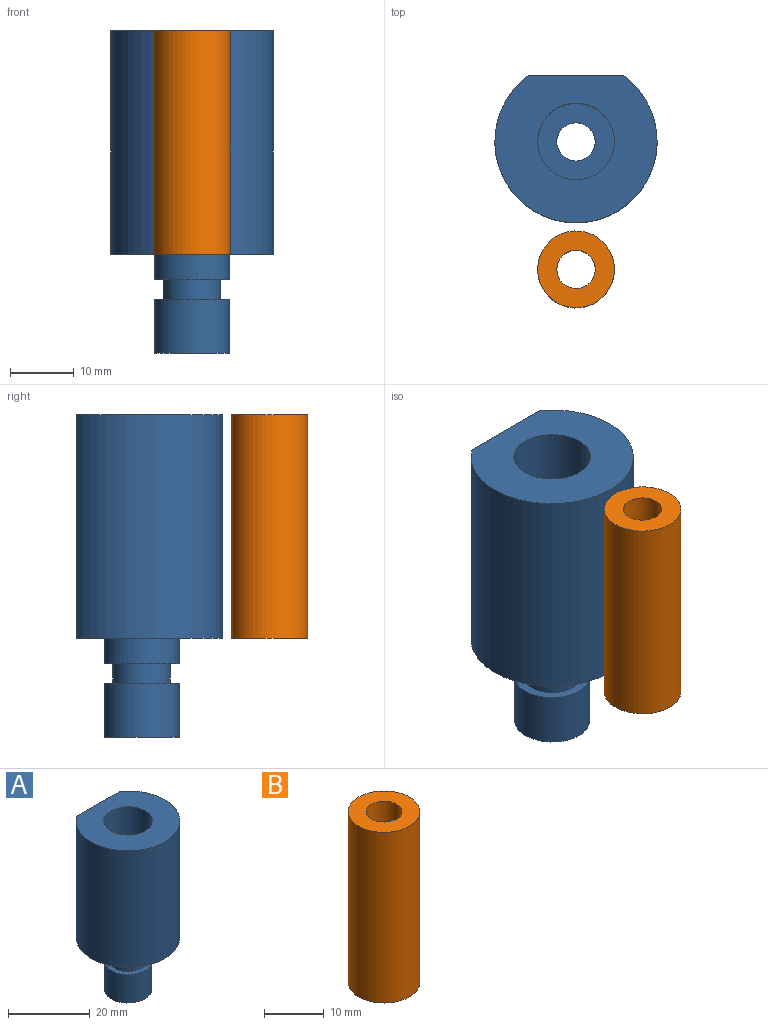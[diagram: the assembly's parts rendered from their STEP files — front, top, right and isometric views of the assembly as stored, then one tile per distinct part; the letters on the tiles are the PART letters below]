
ASSEMBLY  parts=2 mates=1
PART A: 14 faces, bbox 25.4x22.9x50.5 mm
  f0: cylinder r=12.7mm len=35mm, axis (0,0,-1), area 2231.3mm2, adj f1,f2,f13
  f1: plane 25.4x22.95mm, normal (0,0,1), area 368.6mm2, adj f0,f5,f13
  f2: plane 25.4x22.95mm, normal (0,0,-1), area 373.2mm2, adj f0,f7,f13
  f3: cylinder r=4.55mm len=9.1mm, axis (0,-1,0), area 149.8mm2, adj f5,f13
  f4: cylinder r=5.88mm len=11.75mm, axis (0,0,1), area 313.8mm2, adj f8,f10
  f5: cylinder r=6mm len=32mm, axis (0,0,1), area 1135.1mm2, adj f1,f3,f6
  f6: plane 12x12mm, normal (0,0,1), area 84.8mm2, adj f5,f9
  f7: cylinder r=5.88mm len=11.75mm, axis (0,0,1), area 147.7mm2, adj f2,f12
  f8: plane 11.75x11.75mm, normal (0,0,-1), area 80.2mm2, adj f4,f9
  f9: cylinder r=3mm len=18.5mm, axis (0,0,-1), area 348.7mm2, adj f6,f8
  f10: plane 11.75x11.75mm, normal (0,0,1), area 44.8mm2, adj f4,f11
  f11: cylinder r=4.5mm len=9mm, axis (0,0,-1), area 84.8mm2, adj f10,f12
  f12: plane 11.75x11.75mm, normal (0,0,-1), area 44.8mm2, adj f7,f11
  f13: plane 35x15mm, normal (0,1,0), area 460mm2, adj f0,f1,f2,f3
PART B: 4 faces, bbox 12x12x35 mm
  f0: cylinder r=3mm len=35mm, axis (0,0,-1), area 659.7mm2, adj f2,f3
  f1: cylinder r=6mm len=35mm, axis (0,0,-1), area 1319.5mm2, adj f2,f3
  f2: plane 12x12mm, normal (0,0,1), area 84.8mm2, adj f0,f1
  f3: plane 12x12mm, normal (0,0,-1), area 84.8mm2, adj f0,f1
PLACE A t=(-1.02,4.42,-1.57)mm fixed
PLACE B t=(-1.02,-15.58,-1.57)mm
MATE fastened B.f0 <-> A.f1  axis (0,0,1) through (-1.02,-15.58,33.43)mm
